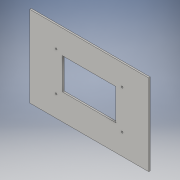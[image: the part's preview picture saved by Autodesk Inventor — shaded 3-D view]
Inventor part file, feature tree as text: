
AUTODESK INVENTOR PART (.ipt)
format: ipt  version: 2016 SP2 (Build 200236200, 236)  size: 173,568 bytes
history: native  units: in
note: dims shown in document units (in); Inventor stores cm internally (conversion verified against a paired STEP export)
features: sketch x3, extrude x2
ambient origin geometry x8: Origin, YZ Plane, XZ Plane, XY Plane, X Axis, Y Axis, Z Axis, Center Point
bodies: Solid1 (feature_tree)
feature tree (5):
  extrude  "Extrusion1"  Depth=5.9055in
  sketch  "Sketch2"  dims[d2=0.1181in d3=0.0in d7=0.126in]
  extrude  "Extrusion2"  Depth=0.1181in
  sketch  "Sketch1"  dims[d0=8.6614in d1=5.9055in]
  sketch  "Sketch3"  dims[d8=0.126in d9=0.126in d10=0.126in d11=3.8976in d12=2.2835in d13=0.4528in d14=0.1969in d15=0.3543in d16=0.126in d17=0.126in d18=0.126in d19=0.126in d20=3.8976in d21=2.2835in d22=0.4528in d23=0.1969in d24=0.3543in d25=0.1181in d26=0.0in]
